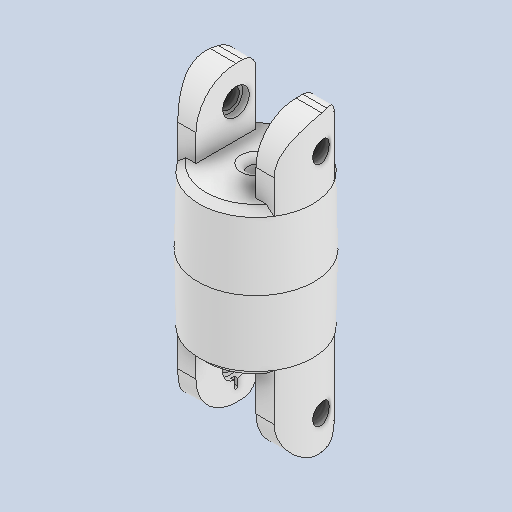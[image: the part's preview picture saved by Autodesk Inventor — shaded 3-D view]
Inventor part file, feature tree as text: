
AUTODESK INVENTOR PART (.ipt)
format: ipt  version: 2022 (Build 260153000, 153)  size: 320,000 bytes
history: native  units: in
note: dims shown in document units (in); Inventor stores cm internally (conversion verified against a paired STEP export)
features: sketch x14, extrude x10, fillet x6, hole x4, chamfer x4, thread x4
ambient origin geometry x8: Origin, YZ Plane, XZ Plane, XY Plane, X Axis, Y Axis, Z Axis, Center Point
bodies: Solid1 (feature_tree)
feature tree (42):
  extrude  "Extrusion1"  Depth=0.6693in
  extrude  "Extrusion2"  Depth=0.0394in TaperAngle=0.0deg
  fillet  "Fillet4"  Radius=0.2362in
  fillet  "Fillet5"  Radius=0.0787in
  hole  "Hole2"  [1 undecoded]
  hole  "Hole3"  [1 undecoded]
  extrude  "Extrusion5"  Depth=0.0197in TaperAngle=0.0deg
  extrude  "Extrusion6"  Depth=0.0394in TaperAngle=45.0deg
  extrude  "Extrusion7"  Depth=0.685in
  extrude  "Extrusion8"  Depth=0.3937in TaperAngle=45.0deg
  chamfer  "Chamfer3"  Distance=0.3937in
  fillet  "Fillet6"  Radius=0.0394in
  extrude  "Extrusion9"  Depth=0.3937in TaperAngle=0.0deg
  chamfer  "Chamfer4"  Distance=0.1969in
  extrude  "Extrusion10"  Depth=0.0394in TaperAngle=45.0deg
  chamfer  "Chamfer5"  Distance=0.2362in
  extrude  "Extrusion11"  Depth=0.2362in TaperAngle=0.0deg
  fillet  "Fillet7"  Radius=0.2362in
  fillet  "Fillet8"  Radius=0.2362in
  fillet  "Fillet9"  Radius=0.0197in
  hole  "Hole4"  [1 undecoded]
  hole  "Hole5"  [1 undecoded]
  chamfer  "Chamfer6"  Distance=0.0344in
  thread  "Thread1"  [1 undecoded]
  thread  "Thread2"  [1 undecoded]
  thread  "Thread3"  [1 undecoded]
  thread  "Thread4"  [1 undecoded]
  sketch  "Sketch1"  dims[d9=0.4724in d10=0.0in d11=0.6693in]
  sketch  "Sketch2"  dims[d12=0.0984in d13=0.0394in d14=0.0in d28=0.2362in d29=0.0787in]
  sketch  "Sketch4"  dims[d30=0.1969in]
  sketch  "Sketch5"  dims[d31=0.1181in d32=0.2362in d33=0.1575in d34=0.0394in d35=90.0deg d36=0.1575in d37=0.0in d38=0.1969in]
  sketch  "Sketch8"  dims[d39=0.1181in d40=0.2362in d41=0.1575in d42=0.0394in d43=90.0deg d44=0.1575in d45=0.0in d61=0.0197in d62=0.0in]
  sketch  "Sketch9"  dims[d63=0.0197in d64=0.0in d68=0.0197in d69=0.0in]
  sketch  "Sketch10"  dims[d70=0.0197in d71=0.0in d72=0.0394in d73=0.0492in d74=45.0deg]
  sketch  "Sketch11"  dims[d75=0.0394in d76=0.685in]
  sketch  "Sketch12"  dims[d77=0.3937in d78=0.0in d79=0.3937in d80=0.0079in d81=45.0deg d82=0.3937in d83=0.0in]
  sketch  "Sketch13"  dims[d84=0.0079in d85=0.3937in d86=45.0deg d87=0.0394in d88=0.0in]
  sketch  "Sketch14"  dims[d89=0.0394in d91=0.0in d92=0.3937in]
  sketch  "Sketch16"  dims[d94=0.0787in]
  sketch  "Sketch17"  dims[d95=0.1969in d96=0.1181in d97=0.2362in d98=0.1575in d99=0.0394in d100=90.0deg d101=0.1575in d102=0.0in d103=0.1969in d104=0.1181in d105=0.2362in d106=0.1575in d107=0.0394in d108=90.0deg d109=0.1575in d110=0.0in d111=0.0394in d112=0.0787in d113=45.0deg d114=0.2362in d115=0.0in d116=0.2362in d117=0.0in d118=0.2362in d119=0.0in d120=0.2362in d121=0.0in d50=0.0197in d51=0.0344in d52=0.0197in d53=0.0344in d90=0.0in]
  sketch  "Sketch15"  dims[d93=0.2362in]
  extrude  "Extrusion12"  [1 undecoded]
note: 9 required parameter values undecoded (feature->parameter linkage not recoverable at this tier; creation-order binding heuristic only, values carry confidence <= 0.55)
